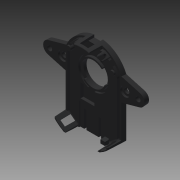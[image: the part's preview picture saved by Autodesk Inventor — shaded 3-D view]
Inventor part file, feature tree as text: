
AUTODESK INVENTOR PART (.ipt)
format: ipt  version: 2016 SP1 (Build 200210100, 210)  size: 1,522,176 bytes
history: native  units: in
note: dims shown in document units (in); Inventor stores cm internally (conversion verified against a paired STEP export)
features: projected_geometry x27, extrude x11, sketch x11, other x1
ambient origin geometry x8: Origin, YZ Plane, XZ Plane, XY Plane, X Axis, Y Axis, Z Axis, Center Point
bodies: Solid1 (feature_tree)
feature tree (50):
  other  "amt102-v"
  extrude  "Extrusion1"  Depth=0.0394in TaperAngle=0.0deg
  extrude  "Extrusion2"  Depth=0.1481in TaperAngle=0.0deg
  sketch  "Sketch3"  dims[d8=0.1063in d9=0.0in d10=0.0438in d11=0.0in]
  extrude  "Extrusion3"  Depth=0.0438in TaperAngle=0.0deg
  sketch  "Sketch4"  dims[d12=0.3937in d13=0.0in d14=0.3937in d15=0.0in]
  extrude  "Extrusion4"  Depth=0.3937in TaperAngle=0.0deg
  extrude  "Extrusion5"  Depth=1.2768in
  sketch  "Sketch5"  dims[d16=0.0394in d17=0.0in d18=1.2768in]
  extrude  "Extrusion6"  Depth=2.0669in
  extrude  "Extrusion7"  Depth=0.113in
  extrude  "Extrusion8"  Depth=0.1181in
  extrude  "Extrusion9"  Depth=0.1969in
  extrude  "Extrusion10"  Depth=0.0394in TaperAngle=0.0deg
  extrude  "Extrusion11"  [1 undecoded]
  sketch  "Sketch1"  dims[d0=0.0438in d1=0.0in d2=0.0394in d3=0.0in]
  projected_geometry  "Projected Loop1"
  projected_geometry  "Projected Loop2"
  projected_geometry  "Projected Loop3"
  projected_geometry  "Projected Loop4"
  projected_geometry  "Projected Loop5"
  projected_geometry  "Projected Loop6"
  projected_geometry  "Projected Loop7"
  projected_geometry  "Projected Loop8"
  projected_geometry  "Projected Loop9"
  sketch  "Sketch2"  dims[d4=0.0394in d5=0.0in d6=0.1481in d7=0.0in]
  projected_geometry  "Projected Loop10"
  projected_geometry  "Projected Loop11"
  projected_geometry  "Projected Loop12"
  projected_geometry  "Projected Loop13"
  projected_geometry  "Projected Loop14"
  projected_geometry  "Projected Loop15"
  projected_geometry  "Projected Loop16"
  projected_geometry  "Projected Loop17"
  projected_geometry  "Projected Loop18"
  projected_geometry  "Projected Loop19"
  sketch  "Sketch6"  dims[d19=1.812in d20=2.0669in]
  sketch  "Sketch7"  dims[d21=0.113in d22=0.113in]
  projected_geometry  "Projected Loop20"
  projected_geometry  "Projected Loop21"
  projected_geometry  "Projected Loop22"
  projected_geometry  "Projected Loop23"
  projected_geometry  "Projected Loop24"
  projected_geometry  "Projected Loop25"
  sketch  "Sketch8"  dims[d23=0.1181in d24=0.1181in]
  projected_geometry  "Projected Loop26"
  sketch  "Sketch9"  dims[d25=0.0984in d26=0.0227in d27=0.1969in]
  projected_geometry  "Projected Loop27"
  sketch  "Sketch10"  dims[d28=0.1969in d29=0.0394in d30=0.0in]
  sketch  "Sketch11"
note: 1 required parameter value undecoded (feature->parameter linkage not recoverable at this tier; creation-order binding heuristic only, values carry confidence <= 0.55)
